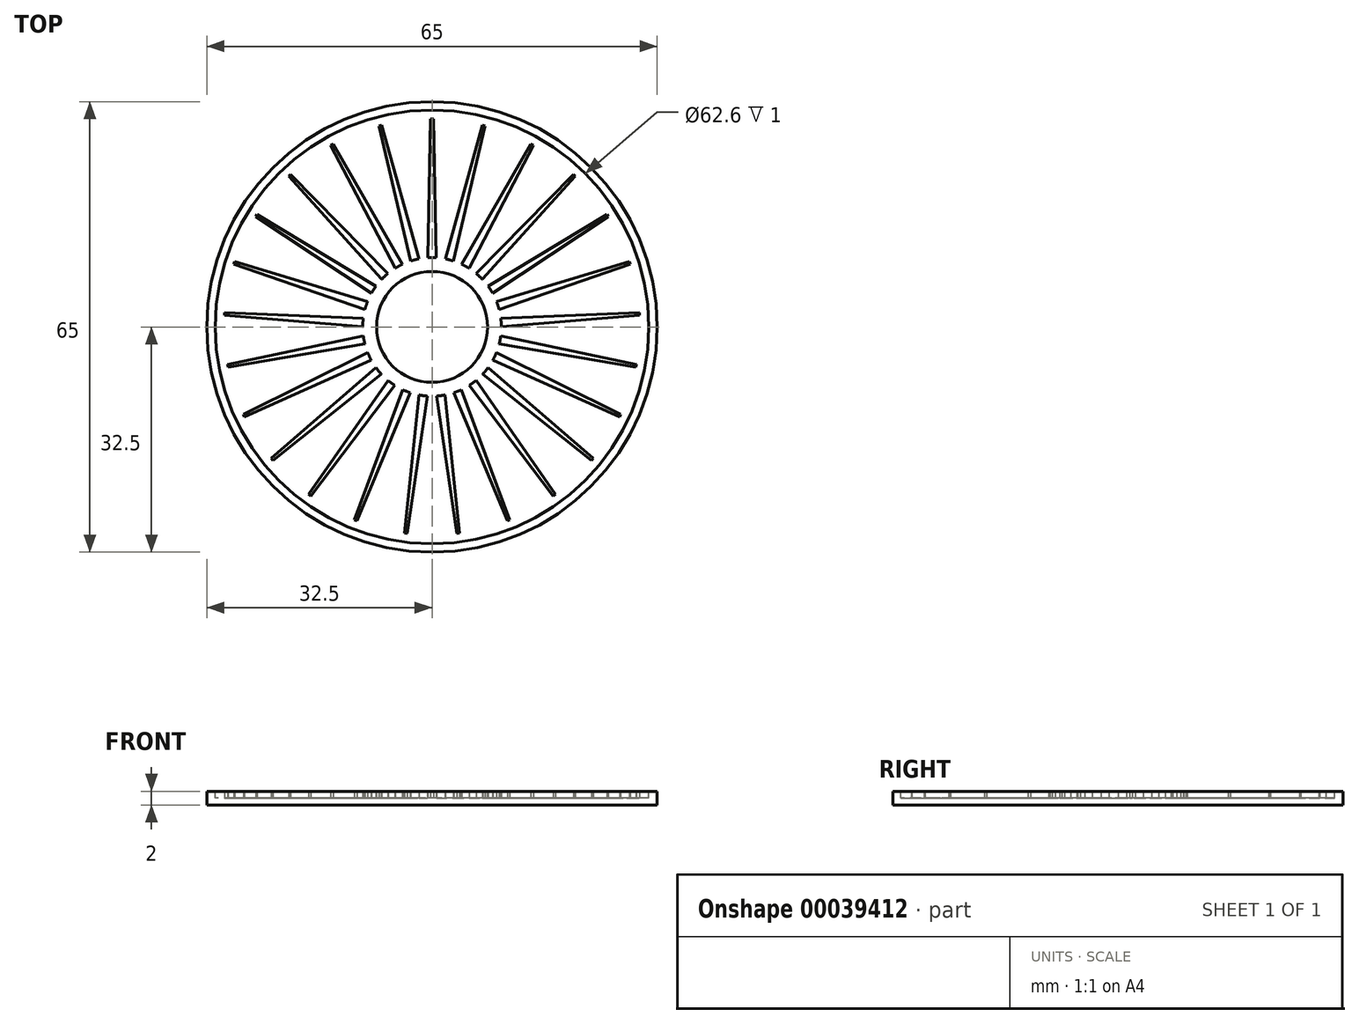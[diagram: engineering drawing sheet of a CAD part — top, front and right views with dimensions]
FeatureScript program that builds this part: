
annotation { "Feature Type Name" : "Feature", "Feature Type Description" : "" }
export const myFeature = defineFeature(function(context is Context, id is Id, definition is map)
    precondition{}
    {
        {
            var Q0;
            Q0=qCreatedBy(makeId("Top.planeOp"),FACE);
            var sketch = newSketch(context, id + "F0", { "sketchPlane" : qUnion([Q0])});
            skCircle(sketch, "E0", {"center": v(0, 0) * mm, "radius": 32.5 * mm});
            skSolve(sketch);
        }
        {
            var Q0;
            Q0=qSketchRegion(id+"F0",true);
            extrude(context, id + "F1", {"entities" : qUnion([Q0]), "depth" : 2 * mm});
        }
        {
            var Q0;
            Q0=makeQuery(id+"F1.opExtrude","CAP_FACE",FACE,{"disambiguationData":[OSD([sQuery(id+"F0.wireOp",EDGE,"E0")])],"isStart":false});
            var sketch = newSketch(context, id + "F2", { "sketchPlane" : qUnion([Q0])});
            skCircle(sketch, "E1", {"center": v(0, 0) * mm, "radius": 31.3 * mm});
            skCircle(sketch, "E2", {"center": v(0, 0) * mm, "radius": 8 * mm});
            skSolve(sketch);
        }
        {
            var Q0;
            Q0=qSketchRegion(id+"F2",true);
            extrude(context, id + "F3", {"entities" : qUnion([Q0]), "operationType" : NewBodyOperationType.REMOVE, "oppositeDirection" : true, "depth" : 1 * mm});
        }
        {
            var Q0;
            Q0=makeQuery(id+"F3.boolean.opBoolean","COPY",FACE,{"derivedFrom":makeQuery(id+"F3.opExtrude","CAP_FACE",FACE,{"disambiguationData":[OSD([sQuery(id+"F2.wireOp",EDGE,"E1"),sQuery(id+"F2.wireOp",EDGE,"E2")])],"isStart":false})});
            var sketch = newSketch(context, id + "F4", { "sketchPlane" : qUnion([Q0])});
            skArc(sketch, "E3", {"start": v(0.6, 9.98) * mm, "mid": v(0, 10) * mm, "end": v(-0.6, 9.98) * mm});
            skLineSegment(sketch, "E4", {"start": v(0, 0) * mm, "end": v(0, 8) * mm, "construction": true});
            skLineSegment(sketch, "E5", {"start": v(0.6, 9.98) * mm, "end": v(0.2, 30) * mm});
            skLineSegment(sketch, "E6", {"start": v(0.2, 30) * mm, "end": v(0, 30) * mm});
            skLineSegment(sketch, "E7", {"start": v(0, 30) * mm, "end": v(-0.2, 30) * mm});
            skLineSegment(sketch, "E8", {"start": v(-0.2, 30) * mm, "end": v(-0.6, 9.98) * mm});
            skSolve(sketch);
        }
        {
            var Q0;
            Q0=qSketchRegion(id+"F4",true);
            var Q1;
            Q1=makeQuery(id+"F3.boolean.opBoolean","SPLIT",FACE,{"disambiguationData":[TD([makeQuery(id+"F3.opExtrude","SWEPT_FACE",FACE,{"disambiguationData":[OSD([sQuery(id+"F2.wireOp",EDGE,"E2")])]})])],"derivedFrom":makeQuery(id+"F1.opExtrude","CAP_FACE",FACE,{"disambiguationData":[OSD([sQuery(id+"F0.wireOp",EDGE,"E0")])],"isStart":false})});
            extrude(context, id + "F5", {"entities" : qUnion([Q0]), "operationType" : NewBodyOperationType.ADD, "endBound" : BoundingType.UP_TO_SURFACE, "endBoundEntityFace" : qUnion([Q1]), "depth" : 25 * mm});
        }
        {
            var Q0;
            Q0=makeQuery(id+"F1.opExtrude","SWEPT_BODY",BODY,{"disambiguationData":[OSD([sQuery(id+"F0.wireOp",EDGE,"E0")])]});
            var Q1;
            Q1=makeQuery(id+"F1.opExtrude","SWEPT_FACE",FACE,{"disambiguationData":[OSD([sQuery(id+"F0.wireOp",EDGE,"E0")])]});
            circularPattern(context, id + "F6", {"operationType" : NewBodyOperationType.ADD, "entities" : qUnion([Q0]), "axis" : qUnion([Q1]), "angle" : 360 * degree, "instanceCount" : 25, "equalSpace" : true});
        }
    });
